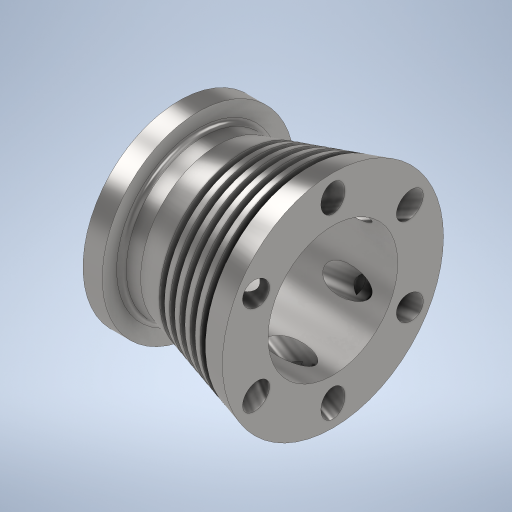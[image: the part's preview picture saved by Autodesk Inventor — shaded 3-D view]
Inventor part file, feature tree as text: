
AUTODESK INVENTOR PART (.ipt)
format: ipt  version: 2024 (Build 280153000, 153)  size: 462,336 bytes
history: native  units: mm
features: sketch x4, plane x3, revolve x2, hole x2, other x2, pattern_linear x1, pattern_circular x1, fillet x1
ambient origin geometry x8: Origin, YZ Plane, XZ Plane, XY Plane, X Axis, Y Axis, Z Axis, Center Point
bodies: Volumenkörper1 (feature_tree)
feature tree (16):
  revolve  "Umdrehung1"
  hole  "Bohrung1"  [1 undecoded]
  plane  "Arbeitsebene2"
  revolve  "Umdrehung2"
  pattern_linear  "Rechteckige Anordnung1"  Count1=4  [1 undecoded]
  plane  "Arbeitsebene4"
  sketch  "Skizze6"  dims[d6=90.0deg d7=27.0mm d8=6.0mm d9=35.0mm d10=9.9mm d11=90.0deg d12=8.0mm d13=0.0mm d15=0.0mm d16=5.0mm d17=1.5mm d19=32.0mm d20=90.0deg d21=50.0mm d23=3.0mm d25=0.0mm d26=60.0deg d27=40.0mm d28=10.0mm d29=10.0mm d30=5.0mm d31=6.0mm d32=4.0mm d33=2.0mm d34=90.0deg d35=8.0mm d36=0.0mm d37=60.0mm d38=360.0deg d40=1.0mm]
  plane  "Arbeitsebene5"
  other  "Arbeitspunkt1"
  other  "Arbeitsachse1"
  hole  "Bohrung2"  [1 undecoded]
  pattern_circular  "Runde Anordnung1"  [2 undecoded]
  fillet  "Rundung1"  Radius=5.0mm
  sketch  "Skizze1"  dims[d0=32.0mm d1=46.0mm]
  sketch  "Skizze2"  dims[d2=4.0mm d3=40.0mm]
  sketch  "Skizze4"  dims[d4=32.0mm d5=4.0mm]
note: 5 required parameter values undecoded (feature->parameter linkage not recoverable at this tier; creation-order binding heuristic only, values carry confidence <= 0.55)
